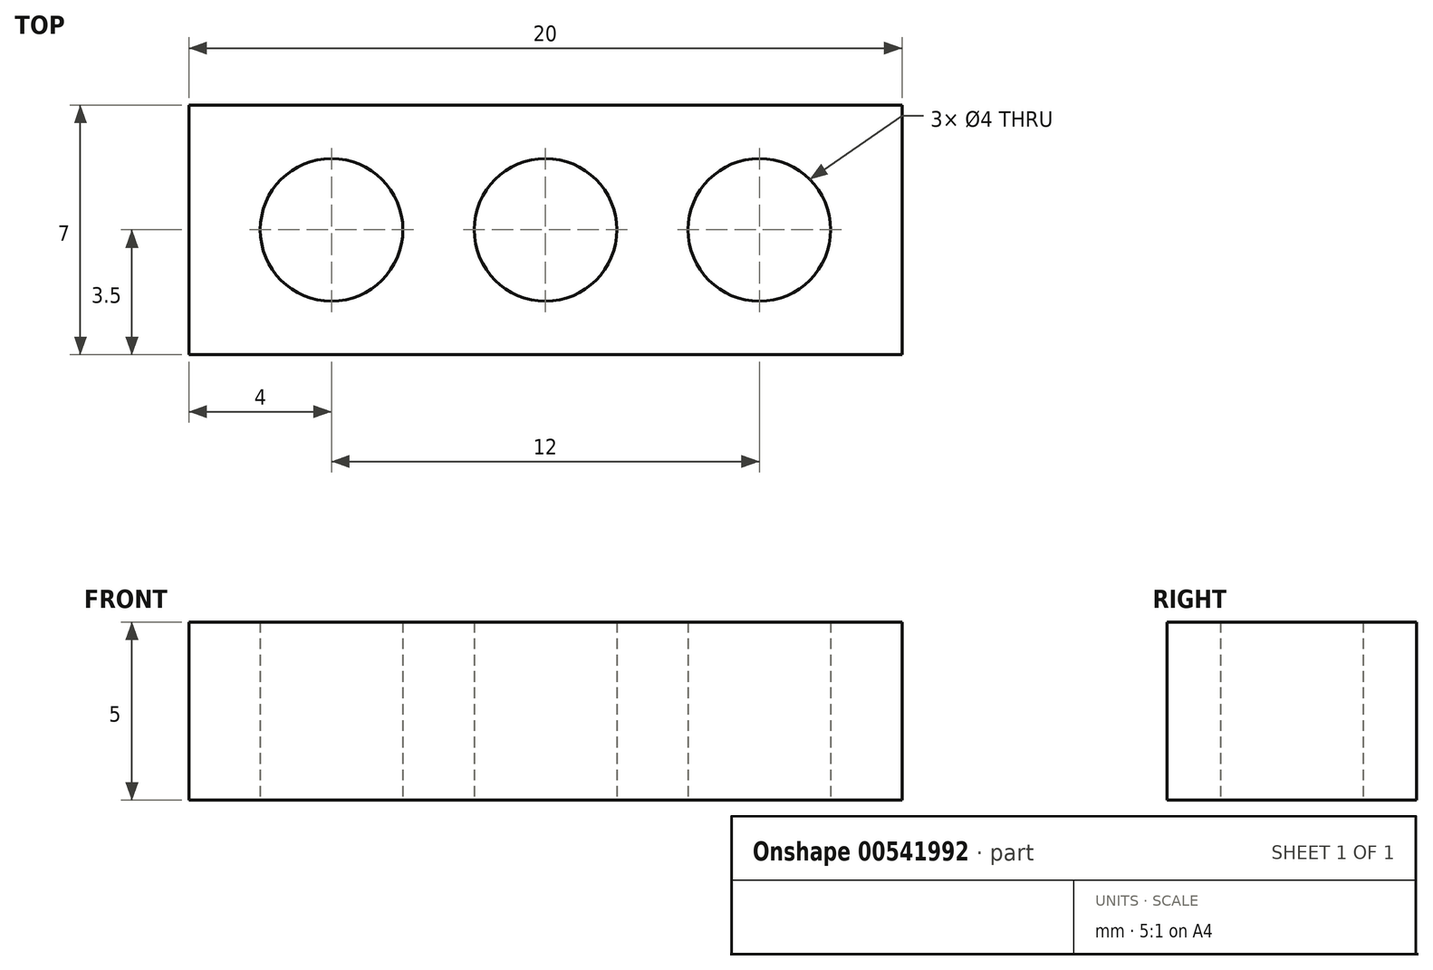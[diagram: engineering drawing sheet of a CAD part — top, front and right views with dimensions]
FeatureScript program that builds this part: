
annotation { "Feature Type Name" : "Feature", "Feature Type Description" : "" }
export const myFeature = defineFeature(function(context is Context, id is Id, definition is map)
    precondition{}
    {
        {
            var Q0;
            Q0=qCreatedBy(makeId("Top.planeOp"),FACE);
            var sketch = newSketch(context, id + "F0", { "sketchPlane" : qUnion([Q0])});
            skLineSegment(sketch, "E0.bottom", {"start": v(10, -3.5) * mm, "end": v(-10, -3.5) * mm});
            skLineSegment(sketch, "E0.top", {"start": v(10, 3.5) * mm, "end": v(-10, 3.5) * mm});
            skLineSegment(sketch, "E0.left", {"start": v(10, -3.5) * mm, "end": v(10, 3.5) * mm});
            skLineSegment(sketch, "E0.right", {"start": v(-10, -3.5) * mm, "end": v(-10, 3.5) * mm});
            skPoint(sketch, "E0.middle", {"position": v(0, 0) * mm});
            skPoint(sketch, "E1.endSnap0", {"position": v(-10, 0) * mm});
            skCircle(sketch, "E2", {"center": v(0, 0) * mm, "radius": 2 * mm});
            skCircle(sketch, "E3", {"center": v(-6, 0) * mm, "radius": 2 * mm});
            skCircle(sketch, "E4", {"center": v(6, 0) * mm, "radius": 2 * mm});
            skSolve(sketch);
        }
        {
            var Q0;
            Q0=makeQuery(id+"F0.imprint","IMPRINT",FACE,{"disambiguationData":[TD([[makeQuery(id+"F0.imprint","IMPRINT",EDGE,{"derivedFrom":sQuery(id+"F0.wireOp",EDGE,"E0.bottom")}),-1.0]])]});
            extrude(context, id + "F1", {"entities" : qUnion([Q0]), "depth" : 5 * mm, "offsetDistance" : 25 * mm});
        }
    });
